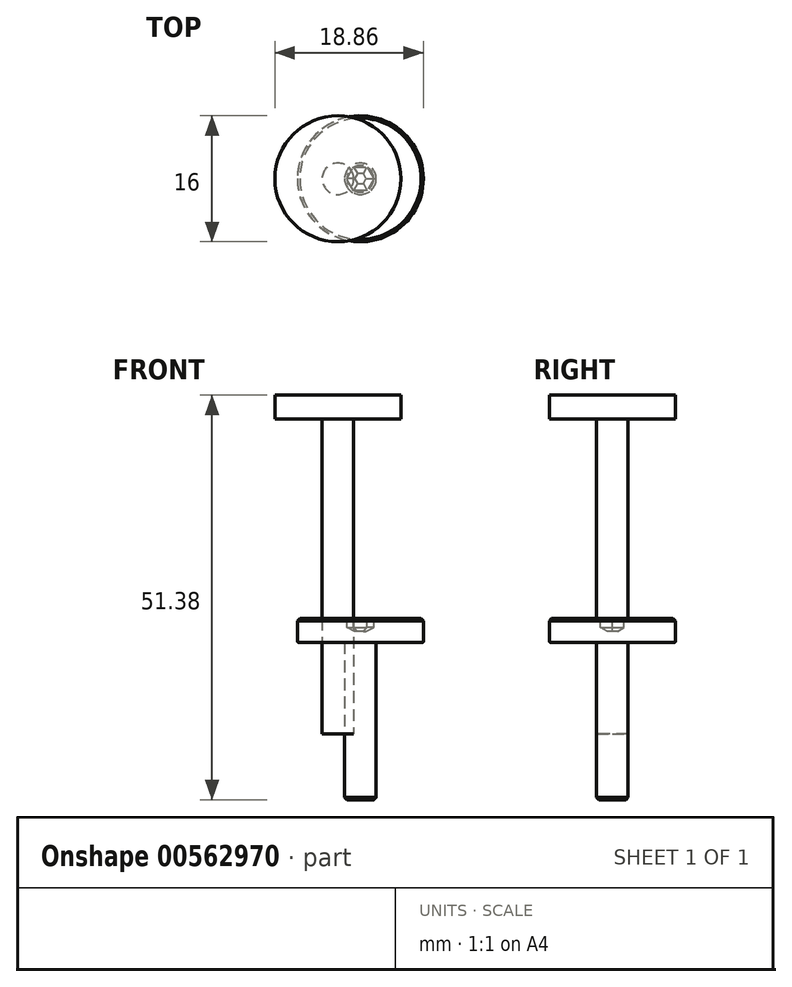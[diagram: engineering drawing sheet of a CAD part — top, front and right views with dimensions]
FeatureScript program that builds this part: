
annotation { "Feature Type Name" : "Feature", "Feature Type Description" : "" }
export const myFeature = defineFeature(function(context is Context, id is Id, definition is map)
    precondition{}
    {
        {
            var Q0;
            Q0=qCreatedBy(makeId("Front.planeOp"),FACE);
            var sketch = newSketch(context, id + "F0", { "sketchPlane" : qUnion([Q0])});
            skLineSegment(sketch, "E0", {"start": v(0, 0) * mm, "end": v(0, -13.37) * mm, "construction": true});
            skLineSegment(sketch, "E1", {"start": v(0, 0) * mm, "end": v(8, 0) * mm});
            skLineSegment(sketch, "E2", {"start": v(8, 0) * mm, "end": v(8, -3) * mm});
            skLineSegment(sketch, "E3", {"start": v(8, -3) * mm, "end": v(2, -3) * mm});
            skLineSegment(sketch, "E4", {"start": v(2, -3) * mm, "end": v(2, -23) * mm});
            skLineSegment(sketch, "E5", {"start": v(2, -23) * mm, "end": v(0, -23) * mm});
            skLineSegment(sketch, "E6", {"start": v(0, -23) * mm, "end": v(0, 0) * mm});
            skSolve(sketch);
        }
        {
            var Q0;
            Q0=qSketchRegion(id+"F0",true);
            var Q1;
            Q1=sQuery(id+"F0.wireOp",EDGE,"E6");
            revolve(context, id + "F1", {"entities" : qUnion([Q0]), "axis" : qUnion([Q1]), "revolveType" : RevolveType.FULL});
        }
        {
            var Q0;
            Q0=makeQuery(id+"F1.opRevolve","SWEPT_FACE",FACE,{"disambiguationData":[OSD([sQuery(id+"F0.wireOp",EDGE,"E1")])]});
            var sketch = newSketch(context, id + "F2", { "sketchPlane" : qUnion([Q0])});
            skCircle(sketch, "E7.cCircle", {"center": v(0, 0) * mm, "radius": 1.5 * mm, "construction": true});
            skLineSegment(sketch, "E7.0", {"start": v(-0.87, 1.5) * mm, "end": v(0.87, 1.5) * mm});
            skLineSegment(sketch, "E7.1", {"start": v(0.87, 1.5) * mm, "end": v(1.73, 0) * mm});
            skLineSegment(sketch, "E7.2", {"start": v(1.73, 0) * mm, "end": v(0.87, -1.5) * mm});
            skLineSegment(sketch, "E7.3", {"start": v(0.87, -1.5) * mm, "end": v(-0.87, -1.5) * mm});
            skLineSegment(sketch, "E7.4", {"start": v(-0.87, -1.5) * mm, "end": v(-1.73, 0) * mm});
            skLineSegment(sketch, "E7.5", {"start": v(-1.73, 0) * mm, "end": v(-0.87, 1.5) * mm});
            skPoint(sketch, "E7.0.midPoint", {"position": v(0, 1.5) * mm});
            skSolve(sketch);
        }
        {
            var Q0;
            Q0=makeQuery(id+"F2.imprint","IMPRINT",FACE,{"disambiguationData":[TD([[makeQuery(id+"F2.imprint","IMPRINT",EDGE,{"derivedFrom":sQuery(id+"F2.wireOp",EDGE,"E7.0")}),-1.0]])]});
            extrude(context, id + "F3", {"entities" : qUnion([Q0]), "operationType" : NewBodyOperationType.REMOVE, "oppositeDirection" : true, "depth" : 1.6 * mm});
        }
        {
            var Q0;
            Q0=makeQuery(id+"F3.boolean.opBoolean","COPY",FACE,{"derivedFrom":makeQuery(id+"F3.opExtrude","CAP_FACE",FACE,{"disambiguationData":[OSD([sQuery(id+"F2.wireOp",EDGE,"E7.0"),sQuery(id+"F2.wireOp",EDGE,"E7.1"),sQuery(id+"F2.wireOp",EDGE,"E7.2"),sQuery(id+"F2.wireOp",EDGE,"E7.3"),sQuery(id+"F2.wireOp",EDGE,"E7.4"),sQuery(id+"F2.wireOp",EDGE,"E7.5")])],"isStart":false})});
            chamfer(context, id + "F4", {"entities" : qUnion([Q0]), "chamferType" : ChamferType.OFFSET_ANGLE, "width" : .5 * mm, "oppositeDirection" : false, "angle" : 60 * degree, "tangentPropagation" : true});
        }
        {
            var Q0;
            Q0=makeQuery(id+"F1.opRevolve","SWEPT_EDGE",EDGE,{"disambiguationData":[OSD([sQuery(id+"F0.wireOp",EDGE,"E1"),sQuery(id+"F0.wireOp",EDGE,"E2")])]});
            var Q1;
            Q1=makeQuery(id+"F1.opRevolve","SWEPT_EDGE",EDGE,{"disambiguationData":[OSD([sQuery(id+"F0.wireOp",EDGE,"E4"),sQuery(id+"F0.wireOp",EDGE,"E5")])]});
            chamfer(context, id + "F5", {"entities" : qUnion([Q0, Q1]), "width" : .3 * mm, "tangentPropagation" : true});
        }
        {
            var Q0;
            Q0=makeQuery(id+"F1.opRevolve","SWEPT_EDGE",EDGE,{"disambiguationData":[OSD([sQuery(id+"F0.wireOp",EDGE,"E2"),sQuery(id+"F0.wireOp",EDGE,"E3")])]});
            fillet(context, id + "F6", {"entities" : qUnion([Q0]), "radius" : .1 * mm, "tangentPropagation" : true, "allowEdgeOverflow" : false});
        }
        {
            var Q0;
            Q0=makeQuery(id+"F1.opRevolve","SWEPT_BODY",BODY,{"disambiguationData":[OSD([sQuery(id+"F0.wireOp",EDGE,"E1"),sQuery(id+"F0.wireOp",EDGE,"E2"),sQuery(id+"F0.wireOp",EDGE,"E3"),sQuery(id+"F0.wireOp",EDGE,"E4"),sQuery(id+"F0.wireOp",EDGE,"E5"),sQuery(id+"F0.wireOp",EDGE,"E6")])]});
            transform(context, id + "F7", {"entities" : qUnion([Q0]), "transformType" : TransformType.COPY});
        }
        {
            var Q0;
            Q0=makeQuery(id+"F7.opPattern","COPY",BODY,{"derivedFrom":makeQuery(id+"F1.opRevolve","SWEPT_BODY",BODY,{"disambiguationData":[OSD([sQuery(id+"F0.wireOp",EDGE,"E1"),sQuery(id+"F0.wireOp",EDGE,"E2"),sQuery(id+"F0.wireOp",EDGE,"E3"),sQuery(id+"F0.wireOp",EDGE,"E4"),sQuery(id+"F0.wireOp",EDGE,"E5"),sQuery(id+"F0.wireOp",EDGE,"E6")])]}),"instanceName":"1"});
            deleteBodies(context, id + "F8", {"entities" : qUnion([Q0])});
        }
        {
            var Q0;
            Q0=qCreatedBy(makeId("Front.planeOp"),FACE);
            var sketch = newSketch(context, id + "F9", { "sketchPlane" : qUnion([Q0])});
            skLineSegment(sketch, "E8", {"start": v(-2.86, 28.38) * mm, "end": v(-2.86, -4.98) * mm, "construction": true});
            skLineSegment(sketch, "E9", {"start": v(-2.86, 28.38) * mm, "end": v(5.14, 28.38) * mm});
            skLineSegment(sketch, "E10", {"start": v(5.14, 28.38) * mm, "end": v(5.14, 25.38) * mm});
            skLineSegment(sketch, "E11", {"start": v(5.14, 25.38) * mm, "end": v(-0.86, 25.38) * mm});
            skLineSegment(sketch, "E12", {"start": v(-0.86, 25.38) * mm, "end": v(-0.86, -14.62) * mm});
            skLineSegment(sketch, "E13", {"start": v(-0.86, -14.62) * mm, "end": v(-2.86, -14.62) * mm});
            skLineSegment(sketch, "E14", {"start": v(-2.86, -14.62) * mm, "end": v(-2.86, 28.38) * mm});
            skSolve(sketch);
        }
        {
            var Q0;
            Q0=makeQuery(id+"F9.imprint","IMPRINT",FACE,{"disambiguationData":[TD([[makeQuery(id+"F9.imprint","IMPRINT",EDGE,{"derivedFrom":sQuery(id+"F9.wireOp",EDGE,"E9")}),-1.0]])]});
            var Q1;
            Q1=sQuery(id+"F9.wireOp",EDGE,"E14");
            revolve(context, id + "F10", {"entities" : qUnion([Q0]), "axis" : qUnion([Q1]), "revolveType" : RevolveType.FULL});
        }
    });
